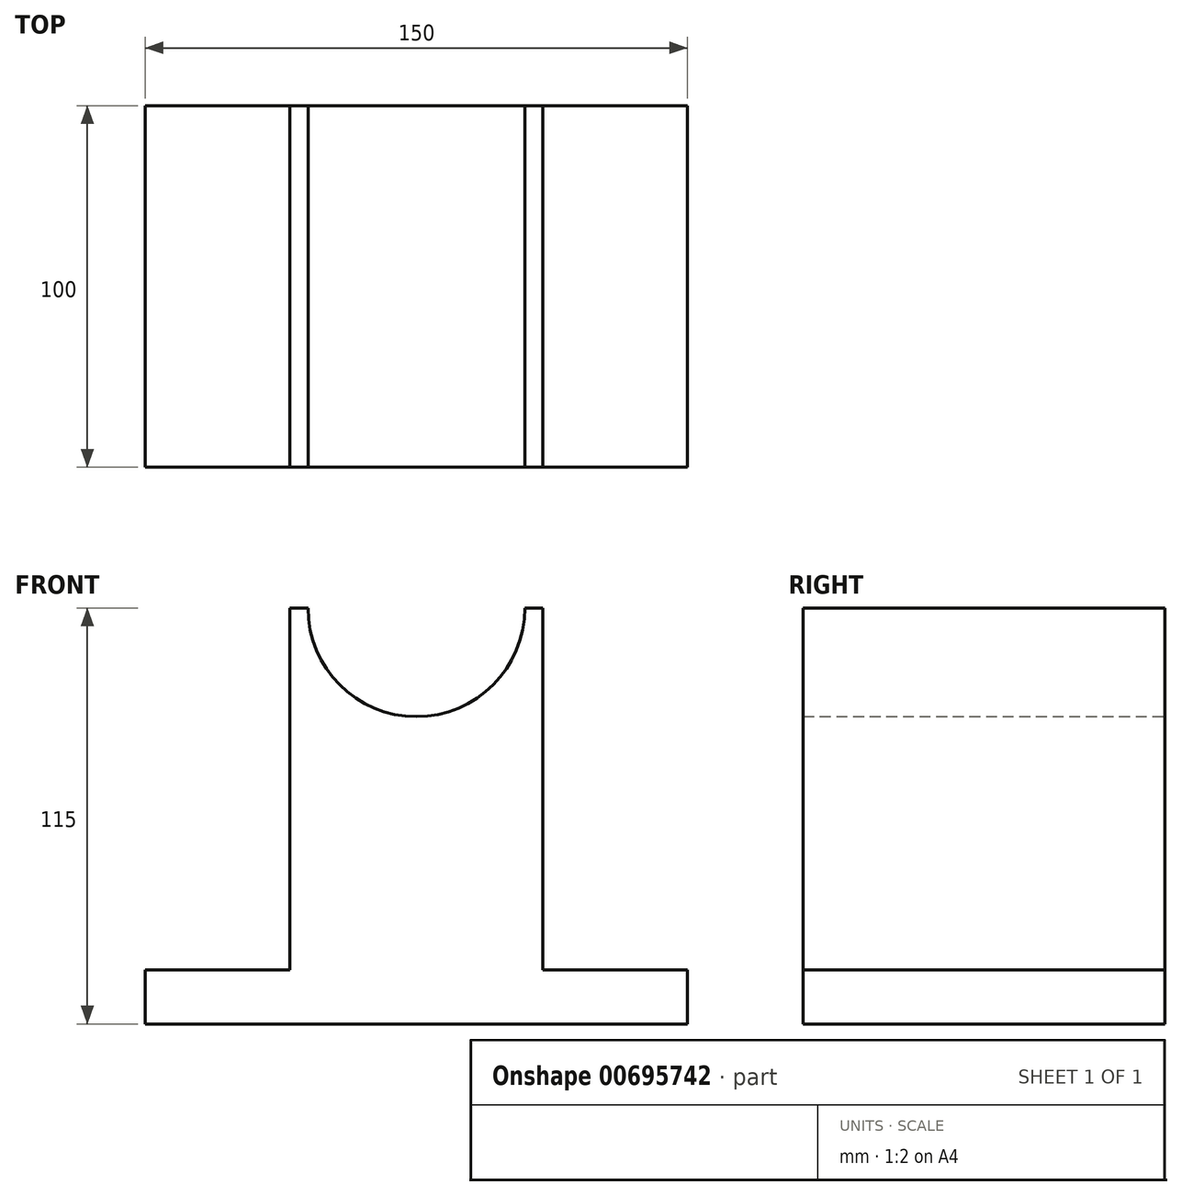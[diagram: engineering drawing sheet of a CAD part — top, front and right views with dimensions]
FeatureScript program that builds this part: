
annotation { "Feature Type Name" : "Feature", "Feature Type Description" : "" }
export const myFeature = defineFeature(function(context is Context, id is Id, definition is map)
    precondition{}
    {
        {
            var Q0;
            Q0=qCreatedBy(makeId("Front.planeOp"),FACE);
            var sketch = newSketch(context, id + "F0", { "sketchPlane" : qUnion([Q0])});
            skLineSegment(sketch, "E0", {"start": v(-110, -17.95) * mm, "end": v(40, -17.95) * mm});
            skLineSegment(sketch, "E1", {"start": v(-70, -17.95) * mm, "end": v(-70, 82.05) * mm});
            skLineSegment(sketch, "E2", {"start": v(0, -17.95) * mm, "end": v(0, 82.05) * mm});
            skLineSegment(sketch, "E3", {"start": v(-70, 82.05) * mm, "end": v(-65, 82.05) * mm});
            skArc(sketch, "E4", {"start": v(-65, 82.05) * mm, "mid": v(-35, 52.05) * mm, "end": v(-5, 82.05) * mm});
            skLineSegment(sketch, "E5.trimOffspring", {"start": v(-5, 82.05) * mm, "end": v(0, 82.05) * mm});
            skLineSegment(sketch, "E6", {"start": v(-110, -17.95) * mm, "end": v(-110, -32.95) * mm});
            skLineSegment(sketch, "E7", {"start": v(-110, -32.95) * mm, "end": v(40, -32.95) * mm});
            skLineSegment(sketch, "E8", {"start": v(40, -17.95) * mm, "end": v(40, -32.95) * mm});
            skSolve(sketch);
        }
        {
            var Q0;
            Q0 = qSketchRegion(id + "F0", true);
            extrude(context, id + "F1", {"entities" : qUnion([Q0]), "depth" : 100 * mm, "offsetDistance" : 25 * mm});
        }
    });
